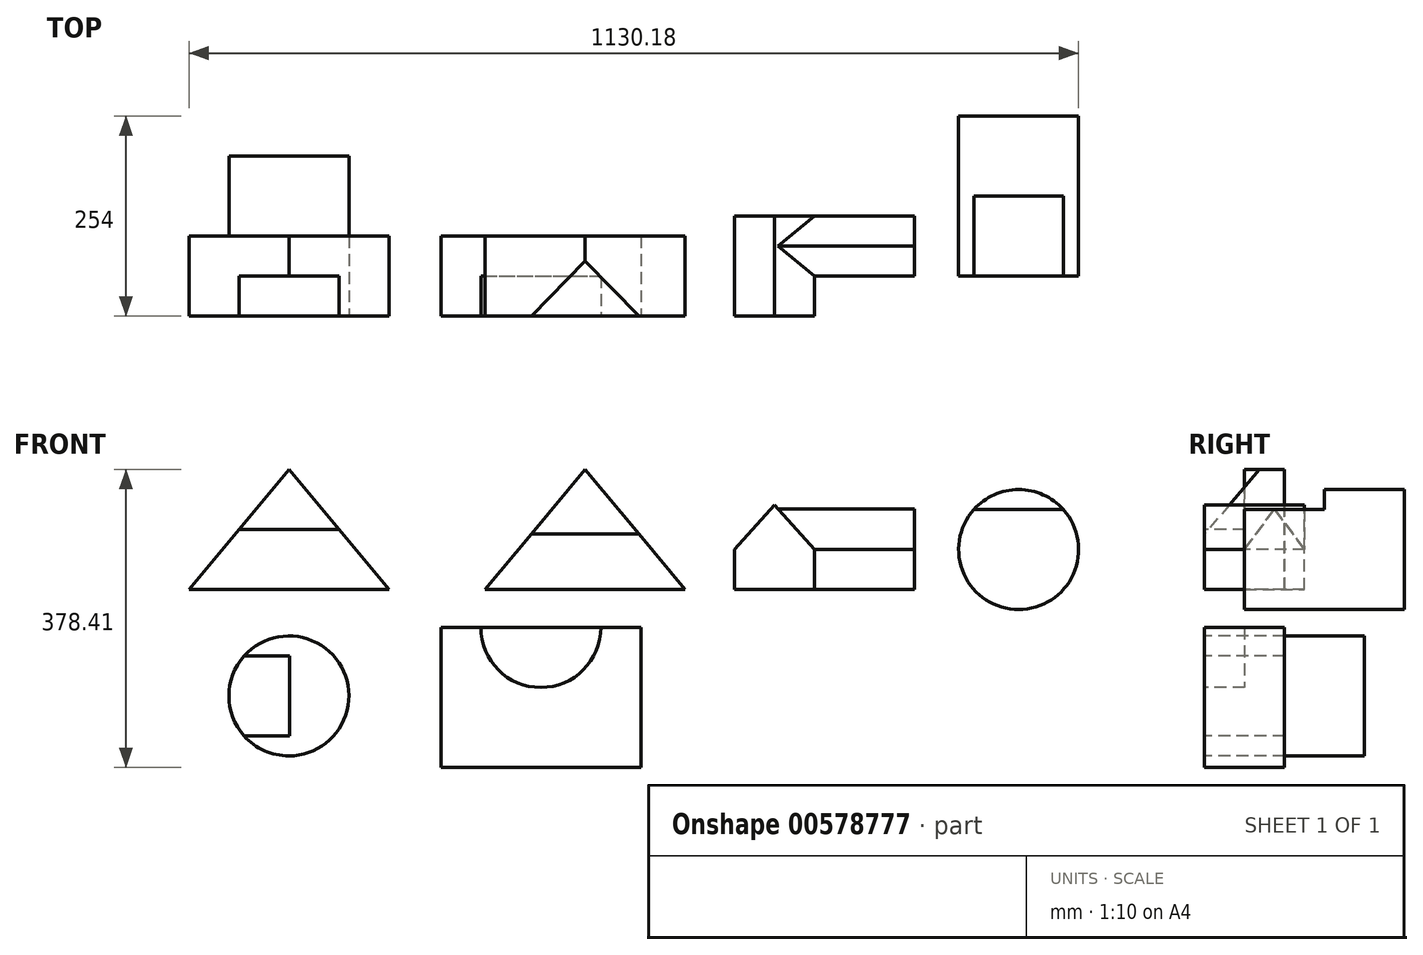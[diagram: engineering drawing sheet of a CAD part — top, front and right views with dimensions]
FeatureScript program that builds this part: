
annotation { "Feature Type Name" : "Feature", "Feature Type Description" : "" }
export const myFeature = defineFeature(function(context is Context, id is Id, definition is map)
    precondition{}
    {
        {
            var Q0;
            Q0=qCreatedBy(makeId("Front.planeOp"),FACE);
            var sketch = newSketch(context, id + "F0", { "sketchPlane" : qUnion([Q0])});
            skLineSegment(sketch, "E0", {"start": v(65.4, 0) * mm, "end": v(319.4, 0) * mm});
            skLineSegment(sketch, "E1", {"start": v(65.4, 0) * mm, "end": v(192.4, 152.4) * mm});
            skLineSegment(sketch, "E2", {"start": v(192.4, 152.4) * mm, "end": v(319.4, 0) * mm});
            skSolve(sketch);
        }
        {
            var Q0;
            Q0=makeQuery(id+"F0.imprint","IMPRINT",FACE,{"disambiguationData":[TD([[makeQuery(id+"F0.imprint","IMPRINT",EDGE,{"derivedFrom":sQuery(id+"F0.wireOp",EDGE,"E0")}),1.0]])]});
            extrude(context, id + "F1", {"entities" : qUnion([Q0]), "oppositeDirection" : true, "depth" : 101.6 * mm, "offsetDistance" : 25.4 * mm});
        }
        {
            var Q0;
            Q0=makeQuery(id+"F1.opExtrude","CAP_FACE",FACE,{"disambiguationData":[OSD([sQuery(id+"F0.wireOp",EDGE,"E0"),sQuery(id+"F0.wireOp",EDGE,"E1"),sQuery(id+"F0.wireOp",EDGE,"E2")])],"isStart":true});
            var sketch = newSketch(context, id + "F2", { "sketchPlane" : qUnion([Q0])});
            skLineSegment(sketch, "E3", {"start": v(128.9, 76.2) * mm, "end": v(255.9, 76.2) * mm});
            skSolve(sketch);
        }
        {
            var Q0;
            {var subQ0=sQuery(id+"F2.wireOp",EDGE,"E3");Q0=makeQuery(id+"F2.imprint","IMPRINT",FACE,{"disambiguationData":[TD([[makeQuery(id+"F2.imprint","IMPRINT",EDGE,{"derivedFrom":subQ0}),1.0]])]});}
            extrude(context, id + "F3", {"entities" : qUnion([Q0]), "operationType" : NewBodyOperationType.REMOVE, "oppositeDirection" : true, "depth" : 50.8 * mm, "offsetDistance" : 25.4 * mm});
        }
        {
            var Q0;
            Q0=makeQuery(id+"F1.opExtrude","CAP_FACE",FACE,{"disambiguationData":[OSD([sQuery(id+"F0.wireOp",EDGE,"E0"),sQuery(id+"F0.wireOp",EDGE,"E1"),sQuery(id+"F0.wireOp",EDGE,"E2")])],"isStart":true});
            var sketch = newSketch(context, id + "F4", { "sketchPlane" : qUnion([Q0])});
            skLineSegment(sketch, "E4", {"start": v(441.8, 0) * mm, "end": v(695.8, 0) * mm});
            skLineSegment(sketch, "E5", {"start": v(441.8, 0) * mm, "end": v(568.8, 152.4) * mm});
            skLineSegment(sketch, "E6", {"start": v(568.8, 152.4) * mm, "end": v(695.8, 0) * mm});
            skSolve(sketch);
        }
        {
            var Q0;
            Q0=makeQuery(id+"F4.imprint","IMPRINT",FACE,{"disambiguationData":[TD([[makeQuery(id+"F4.imprint","IMPRINT",EDGE,{"derivedFrom":sQuery(id+"F4.wireOp",EDGE,"E4")}),1.0]])]});
            extrude(context, id + "F5", {"entities" : qUnion([Q0]), "oppositeDirection" : true, "depth" : 101.6 * mm, "offsetDistance" : 25.4 * mm});
        }
        {
            var Q0;
            Q0=makeQuery(id+"F5.opExtrude","CAP_EDGE",EDGE,{"disambiguationData":[OSD([sQuery(id+"F4.wireOp",EDGE,"E4")])],"isStart":true});
            cPoint(context, id + "F6", {"entities" : qUnion([Q0]), "parameter" : 0.5});
        }
        {
            var Q0;
            Q0=makeQuery(id+"F5.opExtrude","CAP_VERTEX",VERTEX,{"disambiguationData":[OSD([sQuery(id+"F4.wireOp",EDGE,"E5"),sQuery(id+"F4.wireOp",EDGE,"E6")])],"isStart":true});
            var Q1;
            Q1=makeQuery(id+"F5.opExtrude","CAP_VERTEX",VERTEX,{"disambiguationData":[OSD([sQuery(id+"F4.wireOp",EDGE,"E5"),sQuery(id+"F4.wireOp",EDGE,"E6")])],"isStart":false});
            var Q2;
            Q2 = qCreatedBy(id + "F6" ,VERTEX);
            cPlane(context, id + "F7", {"entities" : qUnion([Q0, Q1, Q2]), "cplaneType" : CPlaneType.THREE_POINT, "offset" : 25.4 * mm, "width" : 152.4 * mm, "height" : 152.4 * mm});
        }
        {
            var Q0;
            Q0=qCreatedBy(id+"F7.planeOp",FACE);
            var sketch = newSketch(context, id + "F8", { "sketchPlane" : qUnion([Q0])});
            skLineSegment(sketch, "E7", {"start": v(0, 70.55) * mm, "end": v(69.57, 152.4) * mm});
            skLineSegment(sketch, "E8", {"start": v(69.57, 152.4) * mm, "end": v(0, 152.4) * mm});
            skLineSegment(sketch, "E9", {"start": v(0, 152.4) * mm, "end": v(0, 70.55) * mm});
            skSolve(sketch);
        }
        {
            var Q0;
            Q0 = qSketchRegion(id + "F8", true);
            extrude(context, id + "F9", {"entities" : qUnion([Q0]), "operationType" : NewBodyOperationType.REMOVE, "oppositeDirection" : true, "depth" : 139.7 * mm, "offsetDistance" : 25.4 * mm, "hasSecondDirection" : true, "secondDirectionOppositeDirection" : false, "secondDirectionDepth" : 181.86 * mm});
        }
        {
            var Q0;
            Q0=makeQuery(id+"F5.opExtrude","CAP_FACE",FACE,{"disambiguationData":[OSD([sQuery(id+"F4.wireOp",EDGE,"E4"),sQuery(id+"F4.wireOp",EDGE,"E5"),sQuery(id+"F4.wireOp",EDGE,"E6")])],"isStart":true});
            var sketch = newSketch(context, id + "F10", { "sketchPlane" : qUnion([Q0])});
            skLineSegment(sketch, "E10", {"start": v(758.22, 0) * mm, "end": v(859.82, 0) * mm});
            skLineSegment(sketch, "E11", {"start": v(758.22, 0) * mm, "end": v(758.22, 50.8) * mm});
            skLineSegment(sketch, "E12", {"start": v(758.22, 50.8) * mm, "end": v(809.02, 107.6) * mm});
            skPoint(sketch, "E12.endSnap0", {"position": v(809.02, 0) * mm});
            skLineSegment(sketch, "E13", {"start": v(809.02, 107.6) * mm, "end": v(859.82, 50.8) * mm});
            skLineSegment(sketch, "E14", {"start": v(859.82, 50.8) * mm, "end": v(859.82, 0) * mm});
            skLineSegment(sketch, "E15", {"start": v(859.82, 0) * mm, "end": v(986.82, 0) * mm});
            skLineSegment(sketch, "E16", {"start": v(986.82, 0) * mm, "end": v(986.82, 101.6) * mm});
            skLineSegment(sketch, "E17", {"start": v(986.82, 101.6) * mm, "end": v(814.38, 101.6) * mm});
            skLineSegment(sketch, "E18", {"start": v(859.82, 50.8) * mm, "end": v(986.82, 50.8) * mm});
            skSolve(sketch);
        }
        {
            var Q0;
            Q0=makeQuery(id+"F10.imprint","IMPRINT",FACE,{"disambiguationData":[TD([[makeQuery(id+"F10.imprint","IMPRINT",EDGE,{"derivedFrom":sQuery(id+"F10.wireOp",EDGE,"E10")}),1.0]])]});
            extrude(context, id + "F11", {"entities" : qUnion([Q0]), "oppositeDirection" : true, "depth" : 127 * mm, "offsetDistance" : 25.4 * mm});
        }
        {
            var Q0;
            Q0=makeQuery(id+"F11.opExtrude","SWEPT_FACE",FACE,{"disambiguationData":[OSD([sQuery(id+"F10.wireOp",EDGE,"E14")])]});
            cPlane(context, id + "F12", {"entities" : qUnion([Q0]), "cplaneType" : CPlaneType.OFFSET, "offset" : 127 * mm, "width" : 152.4 * mm, "height" : 152.4 * mm});
        }
        {
            var Q0;
            Q0=qCreatedBy(id+"F12.planeOp",FACE);
            var sketch = newSketch(context, id + "F13", { "sketchPlane" : qUnion([Q0])});
            skLineSegment(sketch, "E19", {"start": v(50.8, 0) * mm, "end": v(127, 0) * mm});
            skLineSegment(sketch, "E20", {"start": v(50.8, 0) * mm, "end": v(50.8, 50.8) * mm});
            skLineSegment(sketch, "E21", {"start": v(127, 0) * mm, "end": v(127, 50.8) * mm});
            skLineSegment(sketch, "E22", {"start": v(127, 50.8) * mm, "end": v(88.9, 102.4) * mm});
            skPoint(sketch, "E22.endSnap0", {"position": v(88.9, 0) * mm});
            skLineSegment(sketch, "E23", {"start": v(88.9, 102.4) * mm, "end": v(50.8, 50.8) * mm});
            skSolve(sketch);
        }
        {
            var Q0;
            Q0=makeQuery(id+"F13.imprint","IMPRINT",FACE,{"disambiguationData":[TD([[makeQuery(id+"F13.imprint","IMPRINT",EDGE,{"derivedFrom":sQuery(id+"F13.wireOp",EDGE,"E19")}),1.0]])]});
            extrude(context, id + "F14", {"entities" : qUnion([Q0]), "operationType" : NewBodyOperationType.ADD, "oppositeDirection" : true, "depth" : 175.26 * mm, "offsetDistance" : 25.4 * mm});
        }
        {
            var Q0;
            Q0=makeQuery(id+"F14.opExtrude","SWEPT_FACE",FACE,{"disambiguationData":[OSD([sQuery(id+"F13.wireOp",EDGE,"E20")])]});
            var sketch = newSketch(context, id + "F15", { "sketchPlane" : qUnion([Q0])});
            skCircle(sketch, "E24", {"center": v(1119.4, 50.8) * mm, "radius": 76.2 * mm});
            skSolve(sketch);
        }
        {
            var Q0;
            Q0=makeQuery(id+"F15.imprint","IMPRINT",FACE,{"disambiguationData":[TD([[makeQuery(id+"F15.imprint","IMPRINT",EDGE,{"derivedFrom":sQuery(id+"F15.wireOp",EDGE,"E24")}),1.0]])]});
            extrude(context, id + "F16", {"entities" : qUnion([Q0]), "oppositeDirection" : true, "depth" : 203.2 * mm, "offsetDistance" : 25.4 * mm});
        }
        {
            var Q0;
            Q0=makeQuery(id+"F16.opExtrude","CAP_FACE",FACE,{"disambiguationData":[OSD([sQuery(id+"F15.wireOp",EDGE,"E24")])],"isStart":true});
            var sketch = newSketch(context, id + "F17", { "sketchPlane" : qUnion([Q0])});
            skLineSegment(sketch, "E25", {"start": v(1062.6, 101.6) * mm, "end": v(1176.2, 101.6) * mm});
            skSolve(sketch);
        }
        {
            var Q0;
            {var subQ0=sQuery(id+"F17.wireOp",EDGE,"E25");Q0=makeQuery(id+"F17.imprint","IMPRINT",FACE,{"disambiguationData":[TD([[makeQuery(id+"F17.imprint","IMPRINT",EDGE,{"derivedFrom":subQ0}),1.0]])]});}
            extrude(context, id + "F18", {"entities" : qUnion([Q0]), "operationType" : NewBodyOperationType.REMOVE, "oppositeDirection" : true, "depth" : 101.6 * mm, "offsetDistance" : 25.4 * mm});
        }
        {
            var Q0;
            Q0=makeQuery(id+"F1.opExtrude","CAP_FACE",FACE,{"disambiguationData":[OSD([sQuery(id+"F0.wireOp",EDGE,"E0"),sQuery(id+"F0.wireOp",EDGE,"E1"),sQuery(id+"F0.wireOp",EDGE,"E2")])],"isStart":true});
            var sketch = newSketch(context, id + "F19", { "sketchPlane" : qUnion([Q0])});
            skCircle(sketch, "E26", {"center": v(192.4, -135.2) * mm, "radius": 76.2 * mm});
            skPoint(sketch, "E26.centerSnap0", {"position": v(192.4, 0) * mm});
            skSolve(sketch);
        }
        {
            var Q0;
            Q0=makeQuery(id+"F19.imprint","IMPRINT",FACE,{"disambiguationData":[TD([[makeQuery(id+"F19.imprint","IMPRINT",EDGE,{"derivedFrom":sQuery(id+"F19.wireOp",EDGE,"E26")}),1.0]])]});
            extrude(context, id + "F20", {"entities" : qUnion([Q0]), "oppositeDirection" : true, "depth" : 203.2 * mm, "offsetDistance" : 25.4 * mm});
        }
        {
            var Q0;
            Q0=makeQuery(id+"F20.opExtrude","CAP_FACE",FACE,{"disambiguationData":[OSD([sQuery(id+"F19.wireOp",EDGE,"E26")])],"isStart":true});
            var sketch = newSketch(context, id + "F21", { "sketchPlane" : qUnion([Q0])});
            skLineSegment(sketch, "E27", {"start": v(135.6, -84.4) * mm, "end": v(193.41, -84.4) * mm});
            skLineSegment(sketch, "E28", {"start": v(193.41, -84.4) * mm, "end": v(193.41, -186) * mm});
            skLineSegment(sketch, "E29", {"start": v(193.41, -186) * mm, "end": v(135.6, -186) * mm});
            skSolve(sketch);
        }
        {
            var Q0;
            {var subQ0=sQuery(id+"F21.wireOp",EDGE,"E27");Q0=makeQuery(id+"F21.imprint","IMPRINT",FACE,{"disambiguationData":[TD([[makeQuery(id+"F21.imprint","IMPRINT",EDGE,{"derivedFrom":subQ0}),-1.0]])]});}
            extrude(context, id + "F22", {"entities" : qUnion([Q0]), "operationType" : NewBodyOperationType.REMOVE, "oppositeDirection" : true, "depth" : 101.6 * mm, "offsetDistance" : 25.4 * mm});
        }
        {
            var Q0;
            Q0=makeQuery(id+"F20.opExtrude","CAP_FACE",FACE,{"disambiguationData":[OSD([sQuery(id+"F19.wireOp",EDGE,"E26")])],"isStart":true});
            var sketch = newSketch(context, id + "F23", { "sketchPlane" : qUnion([Q0])});
            skLineSegment(sketch, "E30", {"start": v(385.45, -226.01) * mm, "end": v(639.45, -226.01) * mm});
            skLineSegment(sketch, "E31", {"start": v(385.45, -226.01) * mm, "end": v(385.45, -48.21) * mm});
            skLineSegment(sketch, "E32", {"start": v(385.45, -48.21) * mm, "end": v(436.25, -48.21) * mm});
            skLineSegment(sketch, "E33", {"start": v(639.45, -226.01) * mm, "end": v(639.45, -48.21) * mm});
            skPoint(sketch, "E34.centerSnap0", {"position": v(512.45, -226.01) * mm});
            skLineSegment(sketch, "E35", {"start": v(588.65, -48.21) * mm, "end": v(639.45, -48.21) * mm});
            skLineSegment(sketch, "E36", {"start": v(436.25, -48.21) * mm, "end": v(588.65, -48.21) * mm});
            skSolve(sketch);
        }
        {
            var Q0;
            Q0=makeQuery(id+"F23.imprint","IMPRINT",FACE,{"disambiguationData":[TD([[makeQuery(id+"F23.imprint","IMPRINT",EDGE,{"derivedFrom":sQuery(id+"F23.wireOp",EDGE,"E30")}),1.0]])]});
            extrude(context, id + "F24", {"entities" : qUnion([Q0]), "oppositeDirection" : true, "depth" : 101.6 * mm, "offsetDistance" : 25.4 * mm});
        }
        {
            var Q0;
            Q0=makeQuery(id+"F24.opExtrude","CAP_FACE",FACE,{"disambiguationData":[OSD([sQuery(id+"F23.wireOp",EDGE,"E30"),sQuery(id+"F23.wireOp",EDGE,"E31"),sQuery(id+"F23.wireOp",EDGE,"E32"),sQuery(id+"F23.wireOp",EDGE,"E33"),sQuery(id+"F23.wireOp",EDGE,"E35"),sQuery(id+"F23.wireOp",EDGE,"E36")])],"isStart":true});
            var sketch = newSketch(context, id + "F25", { "sketchPlane" : qUnion([Q0])});
            skArc(sketch, "E37", {"start": v(436.25, -48.21) * mm, "mid": v(512.45, -124.41) * mm, "end": v(588.65, -48.21) * mm});
            skSolve(sketch);
        }
        {
            var Q0;
            {var subQ0=sQuery(id+"F25.wireOp",EDGE,"E37");Q0=makeQuery(id+"F25.imprint","IMPRINT",FACE,{"disambiguationData":[TD([[makeQuery(id+"F25.imprint","IMPRINT",EDGE,{"derivedFrom":subQ0}),1.0]])]});}
            extrude(context, id + "F26", {"entities" : qUnion([Q0]), "operationType" : NewBodyOperationType.REMOVE, "oppositeDirection" : true, "depth" : 50.8 * mm, "offsetDistance" : 25.4 * mm});
        }
    });
